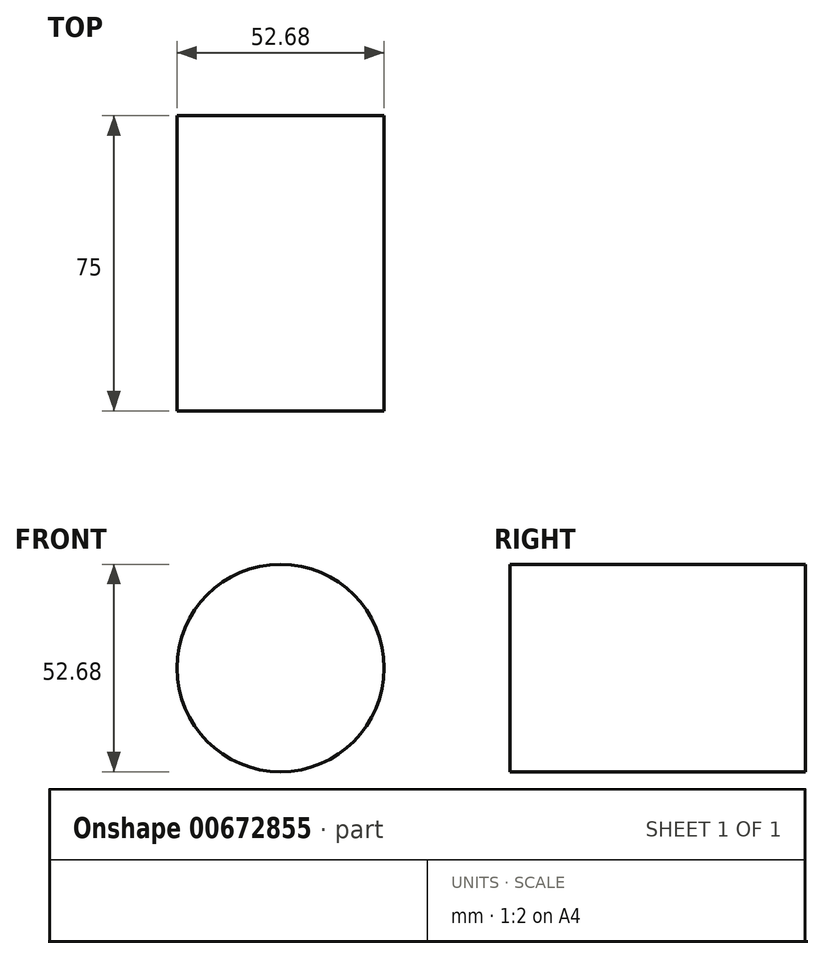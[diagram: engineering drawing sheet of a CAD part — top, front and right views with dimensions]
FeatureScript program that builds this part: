
annotation { "Feature Type Name" : "Feature", "Feature Type Description" : "" }
export const myFeature = defineFeature(function(context is Context, id is Id, definition is map)
    precondition{}
    {
        {
            var Q0;
            Q0=qCreatedBy(makeId("Front.planeOp"),FACE);
            cPlane(context, id + "F0", {"entities" : qUnion([Q0]), "cplaneType" : CPlaneType.OFFSET, "offset" : 25 * mm, "width" : 150 * mm, "height" : 150 * mm});
        }
        {
            var Q0;
            Q0=qCreatedBy(id+"F0.planeOp",FACE);
            cPlane(context, id + "F1", {"entities" : qUnion([Q0]), "cplaneType" : CPlaneType.OFFSET, "offset" : 25 * mm, "width" : 150 * mm, "height" : 150 * mm});
        }
        {
            var Q0;
            Q0=qCreatedBy(id+"F1.planeOp",FACE);
            cPlane(context, id + "F2", {"entities" : qUnion([Q0]), "cplaneType" : CPlaneType.OFFSET, "offset" : 25 * mm, "width" : 150 * mm, "height" : 150 * mm});
        }
        {
            var Q0;
            Q0=qCreatedBy(id+"F2.planeOp",FACE);
            cPlane(context, id + "F3", {"entities" : qUnion([Q0]), "cplaneType" : CPlaneType.OFFSET, "offset" : 25 * mm, "width" : 150 * mm, "height" : 150 * mm});
        }
        {
            var Q0;
            Q0=qCreatedBy(id+"F3.planeOp",FACE);
            cPlane(context, id + "F4", {"entities" : qUnion([Q0]), "cplaneType" : CPlaneType.OFFSET, "offset" : 25 * mm, "width" : 150 * mm, "height" : 150 * mm});
        }
        {
            var Q0;
            Q0=qCreatedBy(id+"F4.planeOp",FACE);
            cPlane(context, id + "F5", {"entities" : qUnion([Q0]), "cplaneType" : CPlaneType.OFFSET, "offset" : 25 * mm, "width" : 150 * mm, "height" : 150 * mm});
        }
        {
            var Q0;
            Q0=qCreatedBy(id+"F3.planeOp",FACE);
            var sketch = newSketch(context, id + "F6", { "sketchPlane" : qUnion([Q0])});
            skCircle(sketch, "E0", {"center": v(0, 0) * mm, "radius": 26.34 * mm});
            skSolve(sketch);
        }
        {
            var Q0;
            Q0=qCreatedBy(id+"F2.planeOp",FACE);
            var sketch = newSketch(context, id + "F7", { "sketchPlane" : qUnion([Q0])});
            skCircle(sketch, "E1", {"center": v(0, 0) * mm, "radius": 26.34 * mm});
            skSolve(sketch);
        }
        {
            var Q0;
            Q0=qCreatedBy(id+"F1.planeOp",FACE);
            var sketch = newSketch(context, id + "F8", { "sketchPlane" : qUnion([Q0])});
            skCircle(sketch, "E2", {"center": v(0, 0) * mm, "radius": 26.34 * mm});
            skSolve(sketch);
        }
        {
            var Q0;
            Q0=qCreatedBy(id+"F0.planeOp",FACE);
            var sketch = newSketch(context, id + "F9", { "sketchPlane" : qUnion([Q0])});
            skCircle(sketch, "E3", {"center": v(0, 0) * mm, "radius": 26.34 * mm});
            skSolve(sketch);
        }
        {
            var Q0;
            Q0=makeQuery(id+"F9.imprint","IMPRINT",FACE,{"disambiguationData":[TD([[makeQuery(id+"F9.imprint","IMPRINT",EDGE,{"derivedFrom":sQuery(id+"F9.wireOp",EDGE,"E3")}),1.0]])]});
            var Q1;
            Q1=makeQuery(id+"F8.imprint","IMPRINT",FACE,{"disambiguationData":[TD([[makeQuery(id+"F8.imprint","IMPRINT",EDGE,{"derivedFrom":sQuery(id+"F8.wireOp",EDGE,"E2")}),1.0]])]});
            var Q2;
            Q2=makeQuery(id+"F7.imprint","IMPRINT",FACE,{"disambiguationData":[TD([[makeQuery(id+"F7.imprint","IMPRINT",EDGE,{"derivedFrom":sQuery(id+"F7.wireOp",EDGE,"E1")}),1.0]])]});
            var Q3;
            Q3=makeQuery(id+"F6.imprint","IMPRINT",FACE,{"disambiguationData":[TD([[makeQuery(id+"F6.imprint","IMPRINT",EDGE,{"derivedFrom":sQuery(id+"F6.wireOp",EDGE,"E0")}),1.0]])]});
            loft(context, id + "F10", {"sheetProfilesArray" : [{ "sheetProfileEntities" : qUnion([Q0]) }, { "sheetProfileEntities" : qUnion([Q1]) }, { "sheetProfileEntities" : qUnion([Q2]) }, { "sheetProfileEntities" : qUnion([Q3]) }]});
        }
    });
